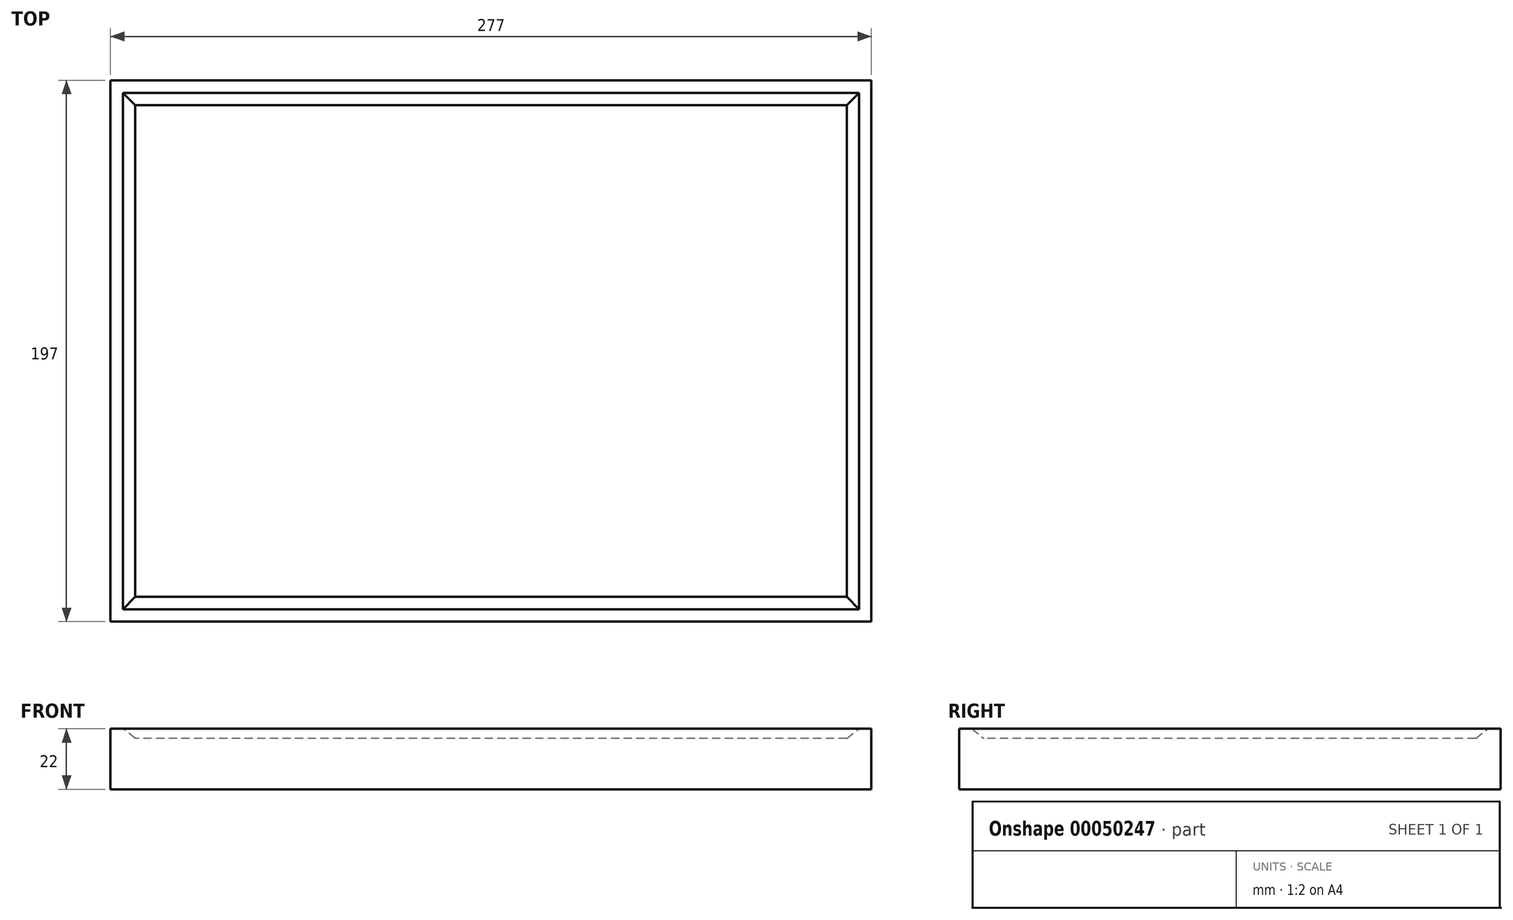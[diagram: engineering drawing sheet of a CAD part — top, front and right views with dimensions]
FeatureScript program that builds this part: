
annotation { "Feature Type Name" : "Feature", "Feature Type Description" : "" }
export const myFeature = defineFeature(function(context is Context, id is Id, definition is map)
    precondition{}
    {
        {
            var Q0;
            Q0=qCreatedBy(makeId("Top.planeOp"),FACE);
            var sketch = newSketch(context, id + "F0", { "sketchPlane" : qUnion([Q0])});
            skLineSegment(sketch, "E0.rect.bottom", {"start": v(138.5, -98.5) * mm, "end": v(-138.5, -98.5) * mm});
            skLineSegment(sketch, "E0.rect.top", {"start": v(138.5, 98.5) * mm, "end": v(-138.5, 98.5) * mm});
            skLineSegment(sketch, "E0.rect.left", {"start": v(138.5, -98.5) * mm, "end": v(138.5, 98.5) * mm});
            skLineSegment(sketch, "E0.rect.right", {"start": v(-138.5, -98.5) * mm, "end": v(-138.5, 98.5) * mm});
            skPoint(sketch, "E0.rect.middle", {"position": v(0, 0) * mm});
            skSolve(sketch);
        }
        {
            var Q0;
            Q0 = qSketchRegion(id + "F0", true);
            var Q1;
            Q1=makeQuery(id+"F0.imprint","IMPRINT",FACE,{"disambiguationData":[TD([[makeQuery(id+"F0.imprint","IMPRINT",EDGE,{"derivedFrom":sQuery(id+"F0.wireOp",EDGE,"E0.rect.bottom")}),-1.0]])]});
            extrude(context, id + "F1", {"entities" : qUnion([Q0, Q1]), "depth" : 22 * mm});
        }
        {
            var Q0;
            Q0=makeQuery(id+"F1.opExtrude","CAP_FACE",FACE,{"disambiguationData":[OSD([sQuery(id+"F0.wireOp",EDGE,"E0.rect.bottom"),sQuery(id+"F0.wireOp",EDGE,"E0.rect.top"),sQuery(id+"F0.wireOp",EDGE,"E0.rect.left"),sQuery(id+"F0.wireOp",EDGE,"E0.rect.right")])],"isStart":false});
            var sketch = newSketch(context, id + "F2", { "sketchPlane" : qUnion([Q0])});
            skLineSegment(sketch, "E1.0", {"start": v(134, 94) * mm, "end": v(-134, 94) * mm});
            skLineSegment(sketch, "E1.1", {"start": v(134, -94) * mm, "end": v(134, 94) * mm});
            skLineSegment(sketch, "E1.2", {"start": v(134, -94) * mm, "end": v(-134, -94) * mm});
            skLineSegment(sketch, "E1.3", {"start": v(-134, -94) * mm, "end": v(-134, 94) * mm});
            skSolve(sketch);
        }
        {
            var Q0;
            Q0 = qSketchRegion(id + "F2", true);
            extrude(context, id + "F3", {"entities" : qUnion([Q0]), "operationType" : NewBodyOperationType.REMOVE, "oppositeDirection" : true, "depth" : 3.5 * mm});
        }
        {
            var Q0;
            Q0=makeQuery(id+"F3.boolean.opBoolean","COPY",FACE,{"derivedFrom":makeQuery(id+"F3.opExtrude","CAP_FACE",FACE,{"disambiguationData":[OSD([sQuery(id+"F2.wireOp",EDGE,"E1.0"),sQuery(id+"F2.wireOp",EDGE,"E1.1"),sQuery(id+"F2.wireOp",EDGE,"E1.2"),sQuery(id+"F2.wireOp",EDGE,"E1.3")])],"isStart":false})});
            chamfer(context, id + "F4", {"entities" : qUnion([Q0]), "chamferType" : ChamferType.OFFSET_ANGLE, "width" : 4.5 * mm, "oppositeDirection" : false, "angle" : 38 * degree, "tangentPropagation" : true});
        }
    });
